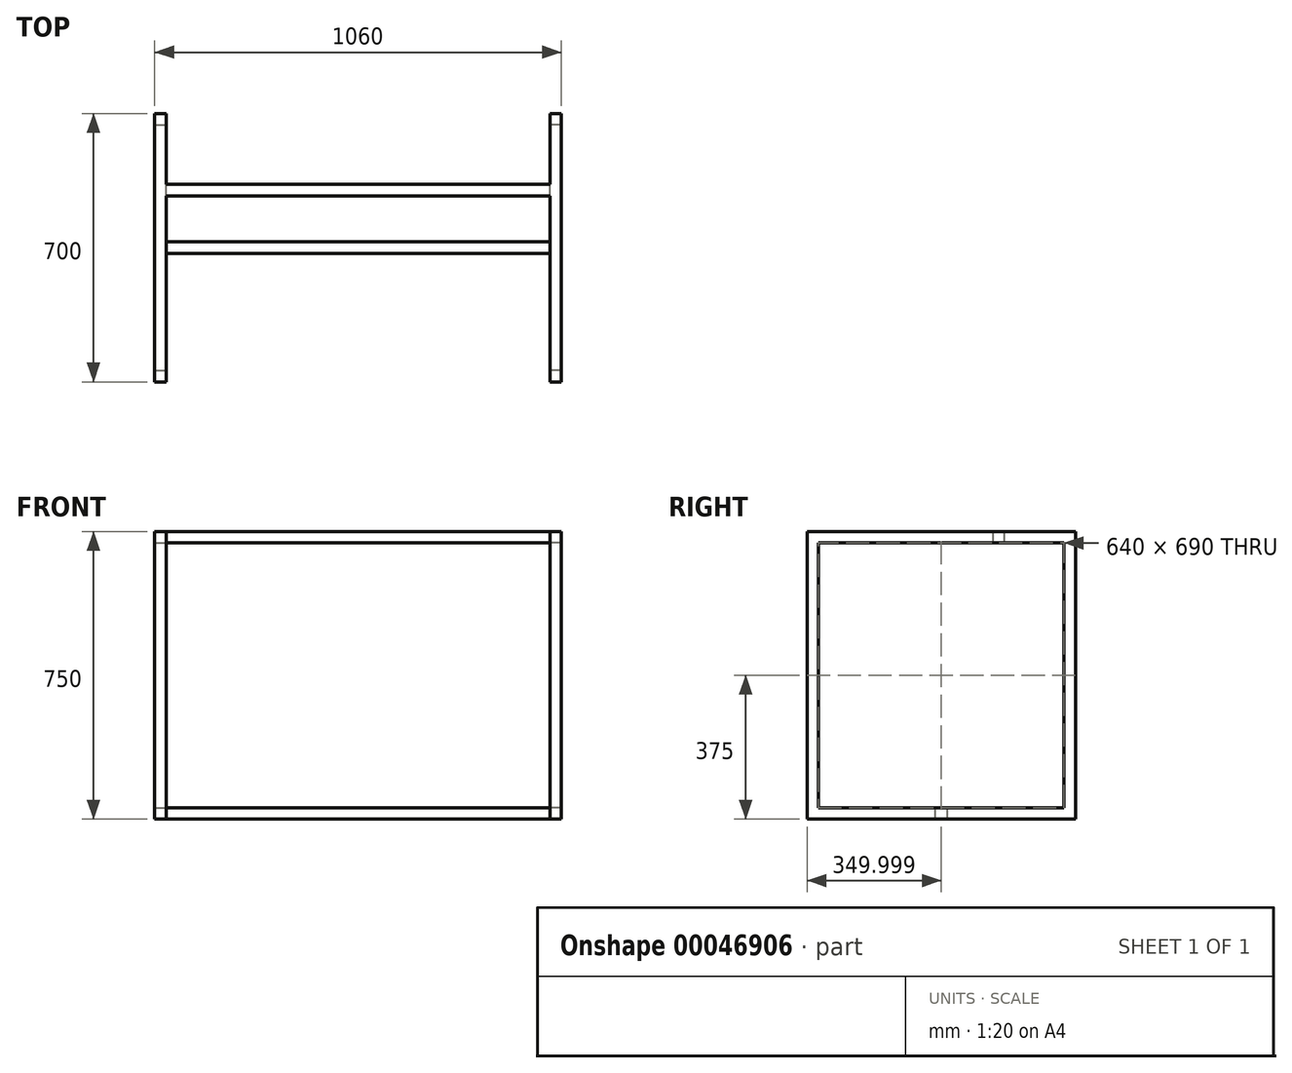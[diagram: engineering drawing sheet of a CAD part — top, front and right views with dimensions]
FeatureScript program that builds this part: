
annotation { "Feature Type Name" : "Feature", "Feature Type Description" : "" }
export const myFeature = defineFeature(function(context is Context, id is Id, definition is map)
    precondition{}
    {
        {
            var Q0;
            Q0=qCreatedBy(makeId("Right.planeOp"),FACE);
            var sketch = newSketch(context, id + "F0", { "sketchPlane" : qUnion([Q0])});
            skLineSegment(sketch, "E0", {"start": v(-493.15, 0) * mm, "end": v(-493.15, -750) * mm});
            skLineSegment(sketch, "E1", {"start": v(-493.15, -750) * mm, "end": v(206.85, -750) * mm});
            skLineSegment(sketch, "E2", {"start": v(206.85, -750) * mm, "end": v(206.85, 0) * mm});
            skLineSegment(sketch, "E3", {"start": v(206.85, 0) * mm, "end": v(-493.15, 0) * mm});
            skLineSegment(sketch, "E4.0", {"start": v(176.85, -30) * mm, "end": v(-463.15, -30) * mm});
            skLineSegment(sketch, "E4.1", {"start": v(176.85, -720) * mm, "end": v(176.85, -30) * mm});
            skLineSegment(sketch, "E4.2", {"start": v(-463.15, -720) * mm, "end": v(176.85, -720) * mm});
            skLineSegment(sketch, "E4.3", {"start": v(-463.15, -30) * mm, "end": v(-463.15, -720) * mm});
            skSolve(sketch);
        }
        {
            var Q0;
            Q0=makeQuery(id+"F0.imprint","IMPRINT",FACE,{"disambiguationData":[TD([[makeQuery(id+"F0.imprint","IMPRINT",EDGE,{"derivedFrom":sQuery(id+"F0.wireOp",EDGE,"E0")}),1.0]])]});
            extrude(context, id + "F1", {"entities" : qUnion([Q0]), "depth" : 30 * mm});
        }
        {
            var Q0;
            Q0=makeQuery(id+"F1.opExtrude","CAP_FACE",FACE,{"disambiguationData":[OSD([sQuery(id+"F0.wireOp",EDGE,"E0"),sQuery(id+"F0.wireOp",EDGE,"E1"),sQuery(id+"F0.wireOp",EDGE,"E2"),sQuery(id+"F0.wireOp",EDGE,"E3"),sQuery(id+"F0.wireOp",EDGE,"E4.0"),sQuery(id+"F0.wireOp",EDGE,"E4.1"),sQuery(id+"F0.wireOp",EDGE,"E4.2"),sQuery(id+"F0.wireOp",EDGE,"E4.3")])],"isStart":true});
            var sketch = newSketch(context, id + "F2", { "sketchPlane" : qUnion([Q0])});
            skLineSegment(sketch, "E5.rect.bottom", {"start": v(8.15, -30) * mm, "end": v(-21.85, -30) * mm});
            skLineSegment(sketch, "E5.rect.top", {"start": v(8.15, 0) * mm, "end": v(-21.85, 0) * mm});
            skLineSegment(sketch, "E5.rect.left", {"start": v(8.15, -30) * mm, "end": v(8.15, 0) * mm});
            skLineSegment(sketch, "E5.rect.right", {"start": v(-21.85, -30) * mm, "end": v(-21.85, 0) * mm});
            skPoint(sketch, "E5.rect.middle", {"position": v(-6.85, -15) * mm});
            skSolve(sketch);
        }
        {
            var Q0;
            Q0=qSketchRegion(id+"F2",true);
            extrude(context, id + "F3", {"entities" : qUnion([Q0]), "operationType" : NewBodyOperationType.ADD, "depth" : 500 * mm});
        }
        {
            var Q0;
            Q0=makeQuery(id+"F1.opExtrude","SWEPT_BODY",BODY,{"disambiguationData":[OSD([sQuery(id+"F0.wireOp",EDGE,"E0"),sQuery(id+"F0.wireOp",EDGE,"E1"),sQuery(id+"F0.wireOp",EDGE,"E2"),sQuery(id+"F0.wireOp",EDGE,"E3"),sQuery(id+"F0.wireOp",EDGE,"E4.0"),sQuery(id+"F0.wireOp",EDGE,"E4.1"),sQuery(id+"F0.wireOp",EDGE,"E4.2"),sQuery(id+"F0.wireOp",EDGE,"E4.3")])]});
            var Q1;
            Q1=makeQuery(id+"F3.opExtrude","CAP_FACE",FACE,{"disambiguationData":[OSD([sQuery(id+"F2.wireOp",EDGE,"E5.rect.bottom"),sQuery(id+"F2.wireOp",EDGE,"E5.rect.top"),sQuery(id+"F2.wireOp",EDGE,"E5.rect.left"),sQuery(id+"F2.wireOp",EDGE,"E5.rect.right")])],"isStart":false});
            mirror(context, id + "F4", {"operationType" : NewBodyOperationType.ADD, "entities" : qUnion([Q0]), "mirrorPlane" : qUnion([Q1])});
        }
        {
            var Q0;
            Q0=makeQuery(id+"F1.opExtrude","CAP_FACE",FACE,{"disambiguationData":[OSD([sQuery(id+"F0.wireOp",EDGE,"E0"),sQuery(id+"F0.wireOp",EDGE,"E1"),sQuery(id+"F0.wireOp",EDGE,"E2"),sQuery(id+"F0.wireOp",EDGE,"E3"),sQuery(id+"F0.wireOp",EDGE,"E4.0"),sQuery(id+"F0.wireOp",EDGE,"E4.1"),sQuery(id+"F0.wireOp",EDGE,"E4.2"),sQuery(id+"F0.wireOp",EDGE,"E4.3")])],"isStart":true});
            var sketch = newSketch(context, id + "F5", { "sketchPlane" : qUnion([Q0])});
            skLineSegment(sketch, "E6", {"start": v(143.15, -750) * mm, "end": v(158.15, -750) * mm});
            skLineSegment(sketch, "E7", {"start": v(158.15, -750) * mm, "end": v(158.15, -720) * mm});
            skLineSegment(sketch, "E8", {"start": v(158.15, -720) * mm, "end": v(128.15, -720) * mm});
            skLineSegment(sketch, "E9", {"start": v(128.15, -720) * mm, "end": v(128.15, -750) * mm});
            skLineSegment(sketch, "E10", {"start": v(128.15, -750) * mm, "end": v(143.15, -750) * mm});
            skSolve(sketch);
        }
        {
            var Q0;
            Q0=qSketchRegion(id+"F5",true);
            extrude(context, id + "F6", {"entities" : qUnion([Q0]), "operationType" : NewBodyOperationType.ADD, "endBound" : BoundingType.UP_TO_NEXT, "depth" : 25 * mm});
        }
    });
